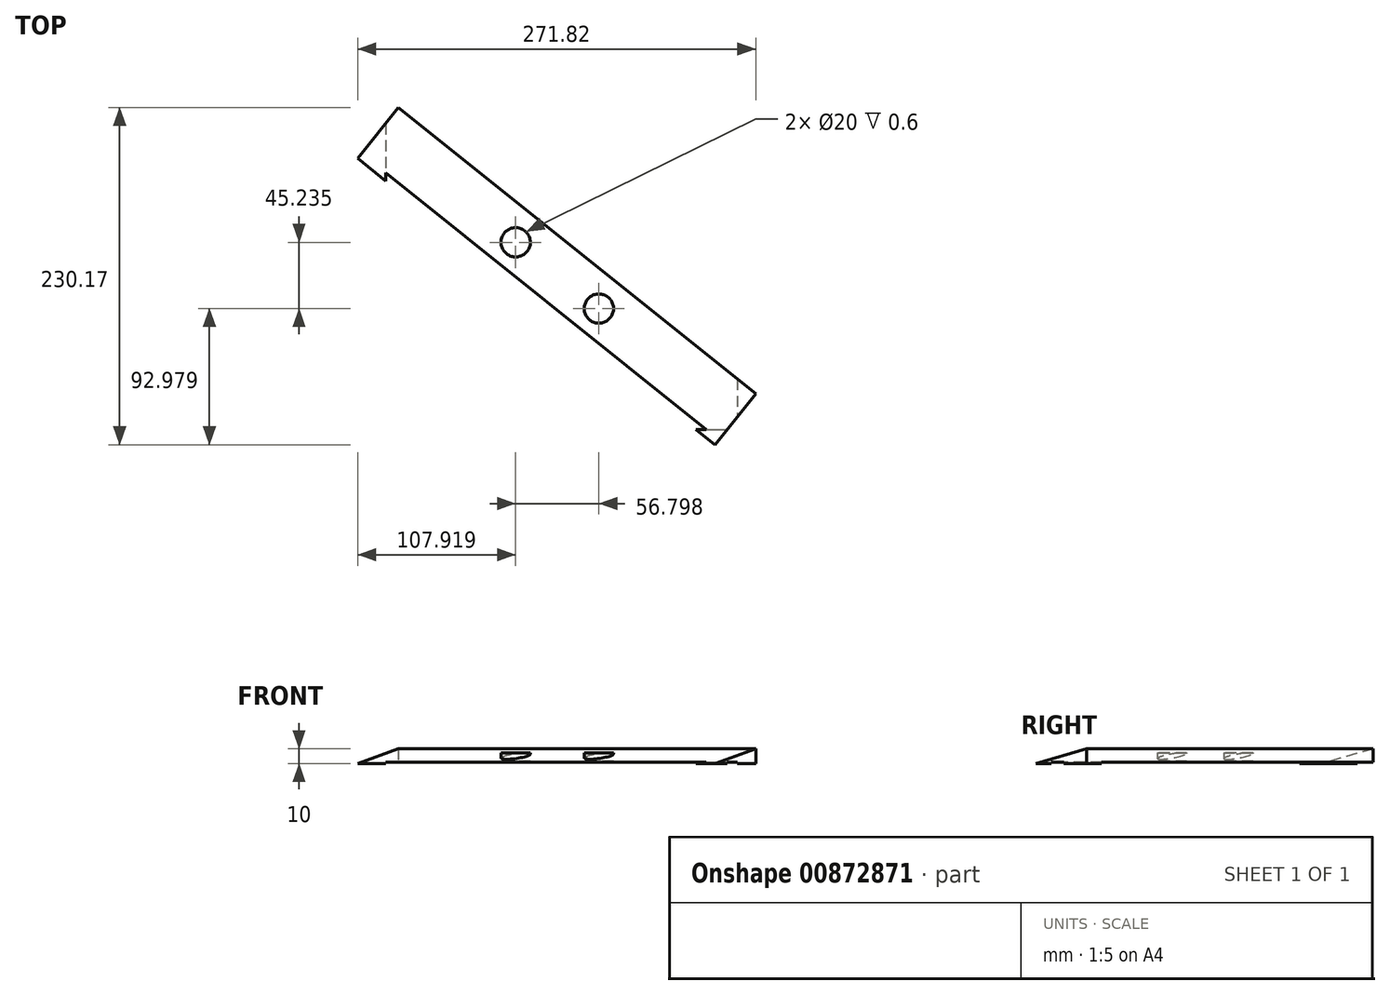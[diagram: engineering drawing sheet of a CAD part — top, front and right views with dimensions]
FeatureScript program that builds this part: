
annotation { "Feature Type Name" : "Feature", "Feature Type Description" : "" }
export const myFeature = defineFeature(function(context is Context, id is Id, definition is map)
    precondition{}
    {
        {
            var Q0;
            Q0=qCreatedBy(makeId("Top.planeOp"),FACE);
            var sketch = newSketch(context, id + "F0", { "sketchPlane" : qUnion([Q0])});
            skLineSegment(sketch, "E0.bottom", {"start": v(-264.2, 336.11) * mm, "end": v(-24.2, 336.11) * mm});
            skLineSegment(sketch, "E0.top", {"start": v(-264.2, 16.11) * mm, "end": v(-24.2, 16.11) * mm});
            skLineSegment(sketch, "E0.left", {"start": v(-264.2, 336.11) * mm, "end": v(-264.2, 16.11) * mm});
            skLineSegment(sketch, "E0.right", {"start": v(-24.2, 336.11) * mm, "end": v(-24.2, 16.11) * mm});
            skLineSegment(sketch, "E1", {"start": v(-264.2, 185.75) * mm, "end": v(-108.6, 61.11) * mm});
            skLineSegment(sketch, "E2", {"start": v(-264.2, 185.75) * mm, "end": v(-143.77, 336.11) * mm});
            skLineSegment(sketch, "E3", {"start": v(-108.6, 61.11) * mm, "end": v(-24.2, 166.48) * mm});
            skLineSegment(sketch, "E4", {"start": v(-24.2, 166.48) * mm, "end": v(-179.81, 291.11) * mm});
            skLineSegment(sketch, "E5.bottom", {"start": v(-268.15, 124.84) * mm, "end": v(-91.45, 345.45) * mm});
            skLineSegment(sketch, "E5.top", {"start": v(-295.47, 146.72) * mm, "end": v(-118.77, 367.33) * mm});
            skLineSegment(sketch, "E5.left", {"start": v(-295.47, 146.72) * mm, "end": v(-268.15, 124.84) * mm});
            skLineSegment(sketch, "E5.right", {"start": v(-118.77, 367.33) * mm, "end": v(-91.45, 345.45) * mm});
            skLineSegment(sketch, "E6.bottom", {"start": v(-255.56, 235.84) * mm, "end": v(-283.38, 201.1) * mm});
            skLineSegment(sketch, "E6.top", {"start": v(-11.56, 40.41) * mm, "end": v(-39.39, 5.67) * mm});
            skLineSegment(sketch, "E6.left", {"start": v(-283.38, 201.1) * mm, "end": v(-39.39, 5.67) * mm});
            skLineSegment(sketch, "E6.right", {"start": v(-255.56, 235.84) * mm, "end": v(-11.56, 40.41) * mm});
            skCircle(sketch, "E7", {"center": v(-175.46, 143.88) * mm, "radius": 10 * mm});
            skCircle(sketch, "E8", {"center": v(-118.66, 98.65) * mm, "radius": 10 * mm});
            skPoint(sketch, "E9", {"position": v(-52.42, 16.11) * mm});
            skSolve(sketch);
        }
        {
            var Q0;
            {var subQ1=sQuery(id+"F0.wireOp",EDGE,"E0.left");var subQ3=sQuery(id+"F0.wireOp",EDGE,"E6.bottom");var subQ4=makeQuery(id+"F0.imprint","INTERSECT",VERTEX,{"derivedFrom":[subQ1,subQ3]});Q0=makeQuery(id+"F0.imprint","IMPRINT",FACE,{"disambiguationData":[TD([[makeQuery(id+"F0.imprint","IMPRINT",EDGE,{"disambiguationData":[TD([[subQ4,1.0]])],"derivedFrom":subQ3}),1.0]])]});}
            var Q1;
            {var subQ1=sQuery(id+"F0.wireOp",EDGE,"E0.left");var subQ3=sQuery(id+"F0.wireOp",EDGE,"E6.bottom");var subQ4=makeQuery(id+"F0.imprint","INTERSECT",VERTEX,{"derivedFrom":[subQ1,subQ3]});Q1=makeQuery(id+"F0.imprint","IMPRINT",FACE,{"disambiguationData":[TD([[makeQuery(id+"F0.imprint","IMPRINT",EDGE,{"disambiguationData":[TD([[subQ4,-1.0]])],"derivedFrom":subQ3}),1.0]])]});}
            var Q2;
            {var subQ1=sQuery(id+"F0.wireOp",EDGE,"E1");var subQ3=sQuery(id+"F0.wireOp",EDGE,"E5.bottom");var subQ4=makeQuery(id+"F0.imprint","INTERSECT",VERTEX,{"derivedFrom":[subQ1,subQ3]});Q2=makeQuery(id+"F0.imprint","IMPRINT",FACE,{"disambiguationData":[TD([[makeQuery(id+"F0.imprint","IMPRINT",EDGE,{"disambiguationData":[TD([[subQ4,-1.0]])],"derivedFrom":subQ3}),1.0]])]});}
            var Q3;
            Q3=makeQuery(id+"F0.imprint","IMPRINT",FACE,{"disambiguationData":[TD([[makeQuery(id+"F0.imprint","IMPRINT",EDGE,{"derivedFrom":sQuery(id+"F0.wireOp",EDGE,"E7")}),-1.0]])]});
            var Q4;
            {var subQ7=sQuery(id+"F0.wireOp",EDGE,"E6.top");var subQ8=sQuery(id+"F0.wireOp",EDGE,"E0.top");var subQ9=makeQuery(id+"F0.imprint","INTERSECT",VERTEX,{"derivedFrom":[subQ8,subQ7]});Q4=makeQuery(id+"F0.imprint","IMPRINT",FACE,{"disambiguationData":[TD([[makeQuery(id+"F0.imprint","IMPRINT",EDGE,{"disambiguationData":[TD([[subQ9,1.0]])],"derivedFrom":subQ8}),1.0]])]});}
            var Q5;
            {var subQ0=sQuery(id+"F0.wireOp",EDGE,"E6.right");var subQ1=sQuery(id+"F0.wireOp",EDGE,"E0.right");var subQ2=makeQuery(id+"F0.imprint","INTERSECT",VERTEX,{"derivedFrom":[subQ1,subQ0]});Q5=makeQuery(id+"F0.imprint","IMPRINT",FACE,{"disambiguationData":[TD([[makeQuery(id+"F0.imprint","IMPRINT",EDGE,{"disambiguationData":[TD([[subQ2,-1.0]])],"derivedFrom":subQ1}),1.0]])]});}
            var Q6;
            {var subQ0=sQuery(id+"F0.wireOp",EDGE,"E6.top");var subQ1=sQuery(id+"F0.wireOp",EDGE,"E0.top");var subQ2=makeQuery(id+"F0.imprint","INTERSECT",VERTEX,{"derivedFrom":[subQ1,subQ0]});Q6=makeQuery(id+"F0.imprint","IMPRINT",FACE,{"disambiguationData":[TD([[makeQuery(id+"F0.imprint","IMPRINT",EDGE,{"disambiguationData":[TD([[subQ2,1.0]])],"derivedFrom":subQ1}),-1.0]])]});}
            extrude(context, id + "F1", {"entities" : qUnion([Q0, Q1, Q2, Q3, Q4, Q5, Q6]), "depth" : 10 * mm, "offsetDistance" : 25 * mm});
        }
        {
            var Q0;
            {var subQ1=sQuery(id+"F0.wireOp",EDGE,"E0.left");var subQ3=sQuery(id+"F0.wireOp",EDGE,"E6.bottom");var subQ4=makeQuery(id+"F0.imprint","INTERSECT",VERTEX,{"derivedFrom":[subQ1,subQ3]});Q0=makeQuery(id+"F0.imprint","IMPRINT",FACE,{"disambiguationData":[TD([[makeQuery(id+"F0.imprint","IMPRINT",EDGE,{"disambiguationData":[TD([[subQ4,1.0]])],"derivedFrom":subQ3}),1.0]])]});}
            var Q1;
            {var subQ1=sQuery(id+"F0.wireOp",EDGE,"E1");var subQ3=sQuery(id+"F0.wireOp",EDGE,"E5.bottom");var subQ4=makeQuery(id+"F0.imprint","INTERSECT",VERTEX,{"derivedFrom":[subQ1,subQ3]});Q1=makeQuery(id+"F0.imprint","IMPRINT",FACE,{"disambiguationData":[TD([[makeQuery(id+"F0.imprint","IMPRINT",EDGE,{"disambiguationData":[TD([[subQ4,-1.0]])],"derivedFrom":subQ3}),1.0]])]});}
            var Q2;
            Q2=makeQuery(id+"F0.imprint","IMPRINT",FACE,{"disambiguationData":[TD([[makeQuery(id+"F0.imprint","IMPRINT",EDGE,{"derivedFrom":sQuery(id+"F0.wireOp",EDGE,"E7")}),-1.0]])]});
            var Q3;
            {var subQ7=sQuery(id+"F0.wireOp",EDGE,"E6.top");var subQ8=sQuery(id+"F0.wireOp",EDGE,"E0.top");var subQ9=makeQuery(id+"F0.imprint","INTERSECT",VERTEX,{"derivedFrom":[subQ8,subQ7]});Q3=makeQuery(id+"F0.imprint","IMPRINT",FACE,{"disambiguationData":[TD([[makeQuery(id+"F0.imprint","IMPRINT",EDGE,{"disambiguationData":[TD([[subQ9,1.0]])],"derivedFrom":subQ8}),1.0]])]});}
            extrude(context, id + "F2", {"entities" : qUnion([Q0, Q1, Q2, Q3]), "operationType" : NewBodyOperationType.REMOVE, "depth" : 1 * mm, "offsetDistance" : 25 * mm});
        }
        {
            var Q0;
            Q0=makeQuery(id+"F1.opExtrude","SWEPT_FACE",FACE,{"disambiguationData":[OSD([sQuery(id+"F0.wireOp",EDGE,"E6.bottom")])]});
            var sketch = newSketch(context, id + "F3", { "sketchPlane" : qUnion([Q0])});
            skLineSegment(sketch, "E10.bottom", {"start": v(-24.32, 10) * mm, "end": v(20.2, 0) * mm});
            skLineSegment(sketch, "E10.top", {"start": v(-17.69, 39.5) * mm, "end": v(26.82, 29.5) * mm});
            skLineSegment(sketch, "E10.left", {"start": v(-24.32, 10) * mm, "end": v(-17.69, 39.5) * mm});
            skLineSegment(sketch, "E10.right", {"start": v(20.2, 0) * mm, "end": v(26.82, 29.5) * mm});
            skSolve(sketch);
        }
        {
            var Q0;
            Q0=makeQuery(id+"F3.imprint","IMPRINT",FACE,{"disambiguationData":[TD([[makeQuery(id+"F3.imprint","IMPRINT",EDGE,{"derivedFrom":sQuery(id+"F3.wireOp",EDGE,"E10.bottom")}),1.0]])]});
            var Q1;
            Q1=makeQuery(id+"F3.imprint","IMPRINT",FACE,{"disambiguationData":[TD([[makeQuery(id+"F3.imprint","IMPRINT",EDGE,{"derivedFrom":sQuery(id+"F3.wireOp",EDGE,"E10.top")}),-1.0]])]});
            extrude(context, id + "F4", {"entities" : qUnion([Q0, Q1]), "operationType" : NewBodyOperationType.REMOVE, "oppositeDirection" : true, "depth" : 345 * mm, "offsetDistance" : 25 * mm});
        }
        {
            var Q0;
            Q0=makeQuery(id+"F0.imprint","IMPRINT",FACE,{"disambiguationData":[TD([[makeQuery(id+"F0.imprint","IMPRINT",EDGE,{"derivedFrom":sQuery(id+"F0.wireOp",EDGE,"E7")}),1.0]])]});
            var Q1;
            Q1=makeQuery(id+"F0.imprint","IMPRINT",FACE,{"disambiguationData":[TD([[makeQuery(id+"F0.imprint","IMPRINT",EDGE,{"derivedFrom":sQuery(id+"F0.wireOp",EDGE,"E8")}),1.0]])]});
            extrude(context, id + "F5", {"entities" : qUnion([Q0, Q1]), "operationType" : NewBodyOperationType.ADD, "depth" : 7.3 * mm, "offsetDistance" : 25 * mm});
        }
        {
            var Q0;
            Q0=makeQuery(id+"F0.imprint","IMPRINT",FACE,{"disambiguationData":[TD([[makeQuery(id+"F0.imprint","IMPRINT",EDGE,{"derivedFrom":sQuery(id+"F0.wireOp",EDGE,"E8")}),1.0]])]});
            var Q1;
            Q1=makeQuery(id+"F0.imprint","IMPRINT",FACE,{"disambiguationData":[TD([[makeQuery(id+"F0.imprint","IMPRINT",EDGE,{"derivedFrom":sQuery(id+"F0.wireOp",EDGE,"E7")}),1.0]])]});
            extrude(context, id + "F6", {"entities" : qUnion([Q0, Q1]), "operationType" : NewBodyOperationType.REMOVE, "depth" : 1.6 * mm, "offsetDistance" : 25 * mm});
        }
    });
